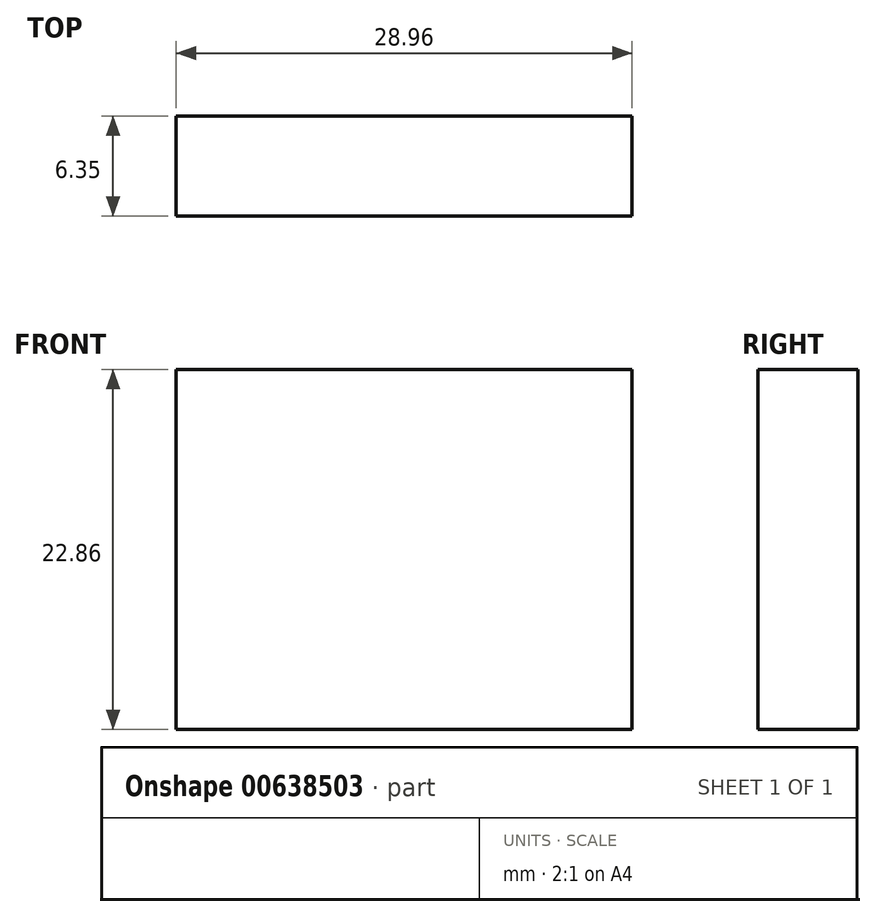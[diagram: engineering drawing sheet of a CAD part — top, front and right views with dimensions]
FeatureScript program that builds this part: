
annotation { "Feature Type Name" : "Feature", "Feature Type Description" : "" }
export const myFeature = defineFeature(function(context is Context, id is Id, definition is map)
    precondition{}
    {
        {
            var Q0;
            Q0=qCreatedBy(makeId("Front.planeOp"),FACE);
            var sketch = newSketch(context, id + "F0", { "sketchPlane" : qUnion([Q0])});
            skLineSegment(sketch, "E0.bottom", {"start": v(57.5, -23.83) * mm, "end": v(28.54, -23.83) * mm});
            skLineSegment(sketch, "E0.top", {"start": v(57.5, -46.69) * mm, "end": v(28.54, -46.69) * mm});
            skLineSegment(sketch, "E0.left", {"start": v(57.5, -23.83) * mm, "end": v(57.5, -46.69) * mm});
            skLineSegment(sketch, "E0.right", {"start": v(28.54, -23.83) * mm, "end": v(28.54, -46.69) * mm});
            skSolve(sketch);
        }
        {
            var Q0;
            Q0 = qSketchRegion(id + "F0", true);
            extrude(context, id + "F1", {"entities" : qUnion([Q0]), "depth" : 6.35 * mm, "offsetDistance" : 25.4 * mm});
        }
    });
